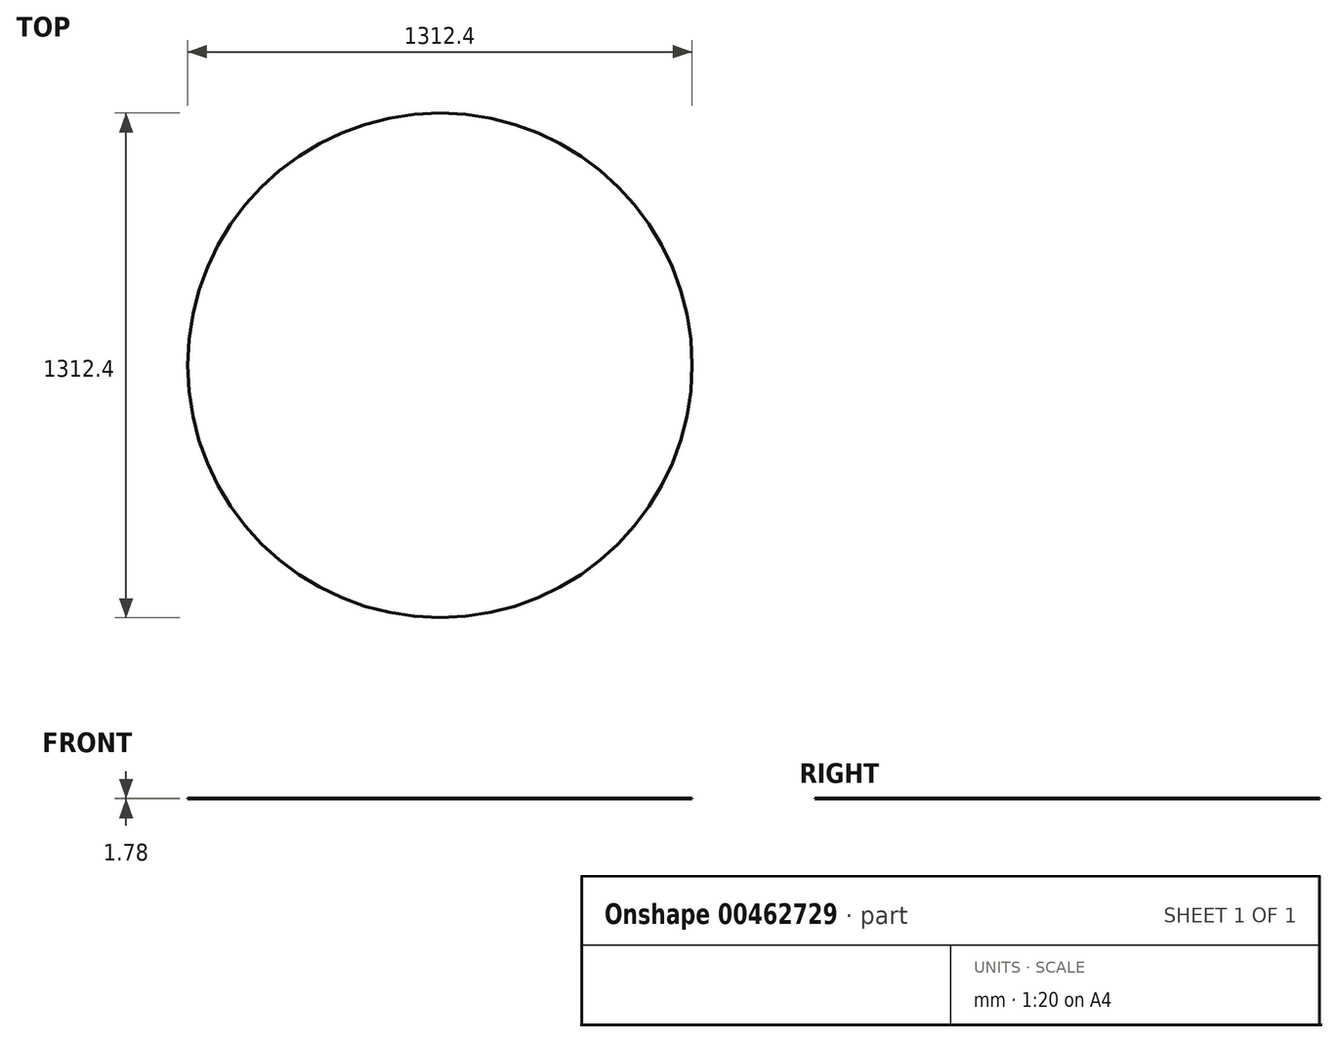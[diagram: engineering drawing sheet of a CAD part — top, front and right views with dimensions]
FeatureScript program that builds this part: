
annotation { "Feature Type Name" : "Feature", "Feature Type Description" : "" }
export const myFeature = defineFeature(function(context is Context, id is Id, definition is map)
    precondition{}
    {
        {
            var Q0;
            Q0=qCreatedBy(makeId("Top.planeOp"),FACE);
            var sketch = newSketch(context, id + "F0", { "sketchPlane" : qUnion([Q0])});
            skCircle(sketch, "E0", {"center": v(0, 0) * mm, "radius": 656.2 * mm});
            skSolve(sketch);
        }
        {
            var Q0;
            Q0=makeQuery(id+"F0.imprint","IMPRINT",FACE,{"disambiguationData":[TD([[makeQuery(id+"F0.imprint","IMPRINT",EDGE,{"derivedFrom":sQuery(id+"F0.wireOp",EDGE,"E0")}),1.0]])]});
            extrude(context, id + "F1", {"entities" : qUnion([Q0]), "depth" : 1.78 * mm});
        }
    });
